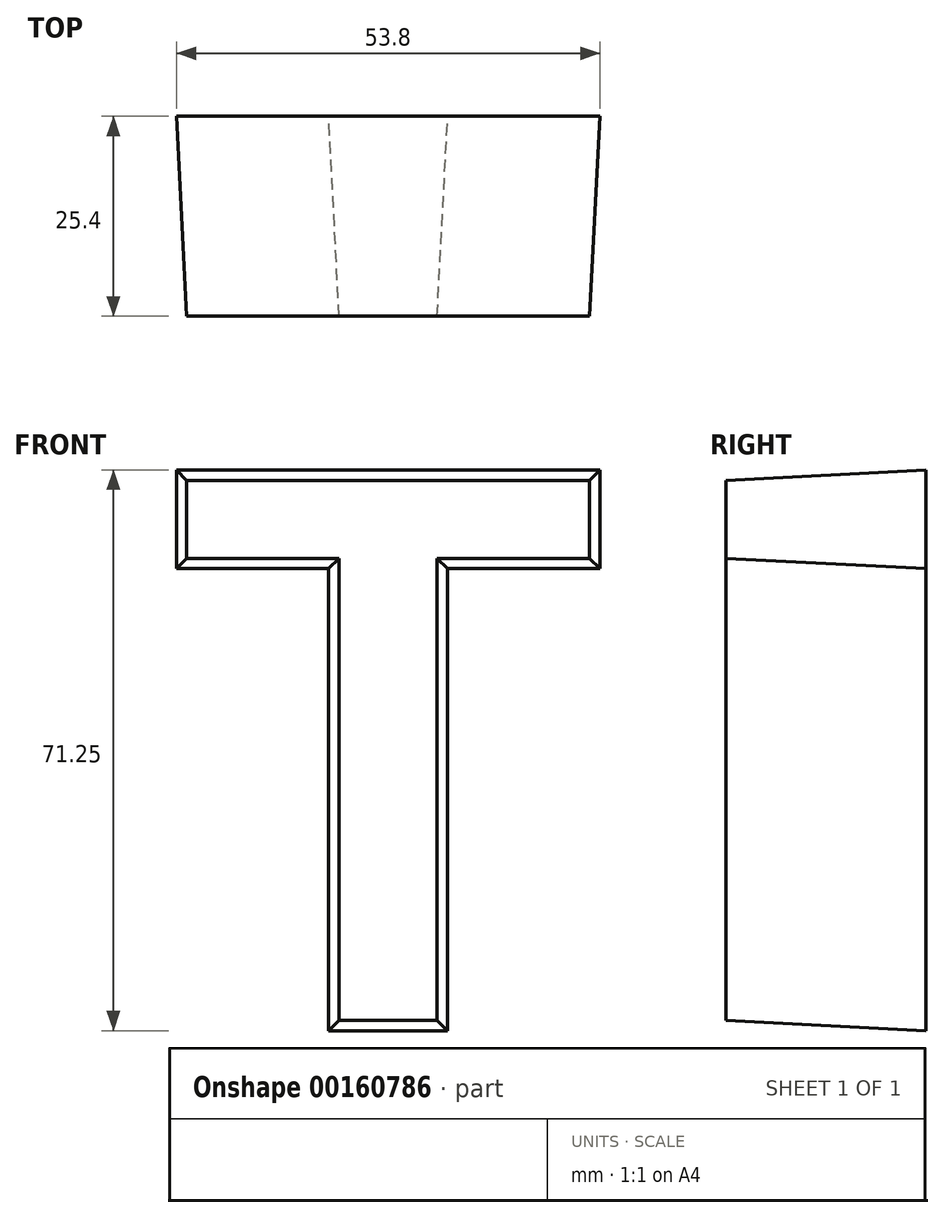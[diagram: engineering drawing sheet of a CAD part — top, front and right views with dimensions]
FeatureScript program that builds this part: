
annotation { "Feature Type Name" : "Feature", "Feature Type Description" : "" }
export const myFeature = defineFeature(function(context is Context, id is Id, definition is map)
    precondition{}
    {
        {
            var Q0;
            Q0=qCreatedBy(makeId("Front.planeOp"),FACE);
            var sketch = newSketch(context, id + "F2", { "sketchPlane" : qUnion([Q0])});
            skText(sketch, "E0", { "text": "Text", "fontName": "OpenSans-Bold.ttf"});
            const initialGuessFwerkLBtWwxFn3lic_0  = {"E0": [-0.04546, -0.03116, 1, 0, 0.07186]};
            skSetInitialGuess(sketch, initialGuessFwerkLBtWwxFn3lic_0);
            skSolve(sketch);
        }
        {
            var Q0;
            Q0 = qSketchRegion(id + "F2", true);
            var sketch = newSketch(context, id + "F0", { "sketchPlane" : qUnion([Q0])});
            skSolve(sketch);
        }
        {
            var Q0;
            Q0=makeQuery(id+"F0.imprint","IMPRINT",FACE,{"disambiguationData":[TD([[makeQuery(id+"F0.imprint","IMPRINT",EDGE,{"derivedFrom":makeQuery(id+"F2.imprint","IMPRINT",EDGE,{"derivedFrom":sQuery(id+"F2.wireOp",EDGE,"E0.sketch_text.stroke-8")})}),-1.0]])]});
            var Q1;
            Q1=makeQuery(id+"F0.imprint","IMPRINT",FACE,{"disambiguationData":[TD([[makeQuery(id+"F0.imprint","IMPRINT",EDGE,{"derivedFrom":makeQuery(id+"F2.imprint","IMPRINT",EDGE,{"derivedFrom":sQuery(id+"F2.wireOp",EDGE,"E0.sketch_text.stroke-0")})}),-1.0]])]});
            var Q2;
            Q2=makeQuery(id+"F0.imprint","IMPRINT",FACE,{"disambiguationData":[TD([[makeQuery(id+"F0.imprint","IMPRINT",EDGE,{"derivedFrom":makeQuery(id+"F2.imprint","IMPRINT",EDGE,{"derivedFrom":sQuery(id+"F2.wireOp",EDGE,"E0.sketch_text.stroke-28")})}),-1.0]])]});
            var Q3;
            Q3=makeQuery(id+"F0.imprint","IMPRINT",FACE,{"disambiguationData":[TD([[makeQuery(id+"F0.imprint","IMPRINT",EDGE,{"derivedFrom":makeQuery(id+"F2.imprint","IMPRINT",EDGE,{"derivedFrom":sQuery(id+"F2.wireOp",EDGE,"E0.sketch_text.stroke-40")})}),-1.0]])]});
            extrude(context, id + "F1", {"entities" : qUnion([Q0, Q1, Q2, Q3]), "depth" : 25.4 * mm, "hasDraft" : true, "draftAngle" : 3 * degree, "draftPullDirection" : true});
        }
    });
